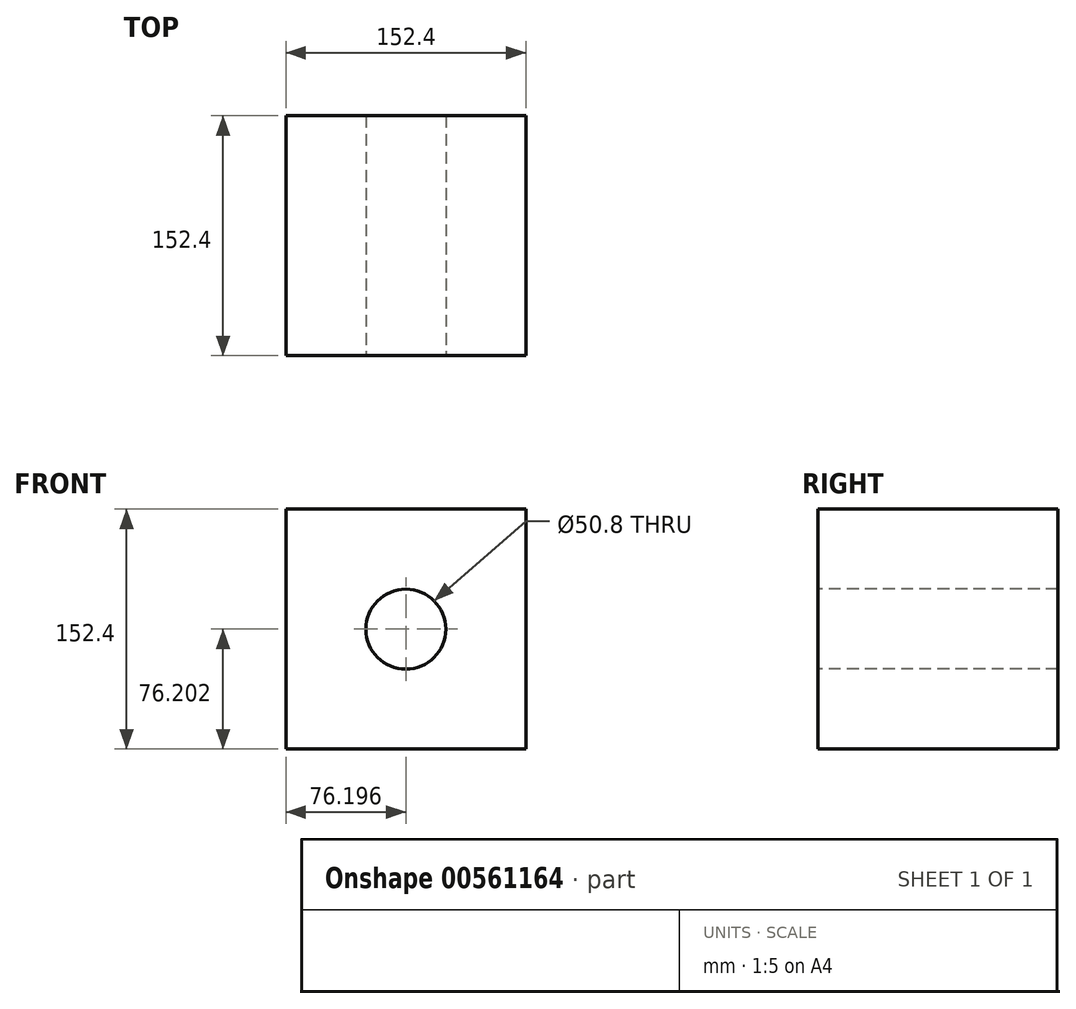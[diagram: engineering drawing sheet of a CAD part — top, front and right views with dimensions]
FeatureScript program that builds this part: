
annotation { "Feature Type Name" : "Feature", "Feature Type Description" : "" }
export const myFeature = defineFeature(function(context is Context, id is Id, definition is map)
    precondition{}
    {
        {
            var Q0;
            Q0=qCreatedBy(makeId("Front.planeOp"),FACE);
            var sketch = newSketch(context, id + "F0", { "sketchPlane" : qUnion([Q0])});
            skLineSegment(sketch, "E0.bottom", {"start": v(-101.66, 84.53) * mm, "end": v(50.74, 84.53) * mm});
            skLineSegment(sketch, "E0.top", {"start": v(-101.66, -67.87) * mm, "end": v(50.74, -67.87) * mm});
            skLineSegment(sketch, "E0.left", {"start": v(-101.66, 84.53) * mm, "end": v(-101.66, -67.87) * mm});
            skLineSegment(sketch, "E0.right", {"start": v(50.74, 84.53) * mm, "end": v(50.74, -67.87) * mm});
            skSolve(sketch);
        }
        {
            var Q0;
            Q0=makeQuery(id+"F0.imprint","IMPRINT",FACE,{"disambiguationData":[TD([[makeQuery(id+"F0.imprint","IMPRINT",EDGE,{"derivedFrom":sQuery(id+"F0.wireOp",EDGE,"E0.bottom")}),-1.0]])]});
            extrude(context, id + "F1", {"entities" : qUnion([Q0]), "depth" : 152.4 * mm, "offsetDistance" : 25.4 * mm});
        }
        {
            var Q0;
            Q0=makeQuery(id+"F1.opExtrude","CAP_FACE",FACE,{"disambiguationData":[OSD([sQuery(id+"F0.wireOp",EDGE,"E0.bottom"),sQuery(id+"F0.wireOp",EDGE,"E0.top"),sQuery(id+"F0.wireOp",EDGE,"E0.left"),sQuery(id+"F0.wireOp",EDGE,"E0.right")])],"isStart":false});
            var sketch = newSketch(context, id + "F2", { "sketchPlane" : qUnion([Q0])});
            skCircle(sketch, "E1", {"center": v(-25.46, 8.33) * mm, "radius": 25.4 * mm});
            skPoint(sketch, "E1.centerSnap0", {"position": v(-101.66, 8.33) * mm});
            skPoint(sketch, "E1.centerSnap1", {"position": v(-25.46, -67.87) * mm});
            skSolve(sketch);
        }
        {
            var Q0;
            Q0=makeQuery(id+"F2.imprint","IMPRINT",FACE,{"disambiguationData":[TD([[makeQuery(id+"F2.imprint","IMPRINT",EDGE,{"derivedFrom":sQuery(id+"F2.wireOp",EDGE,"E1")}),1.0]])]});
            extrude(context, id + "F3", {"entities" : qUnion([Q0]), "operationType" : NewBodyOperationType.REMOVE, "endBound" : BoundingType.THROUGH_ALL, "oppositeDirection" : true, "depth" : 25.4 * mm, "offsetDistance" : 25.4 * mm});
        }
    });
